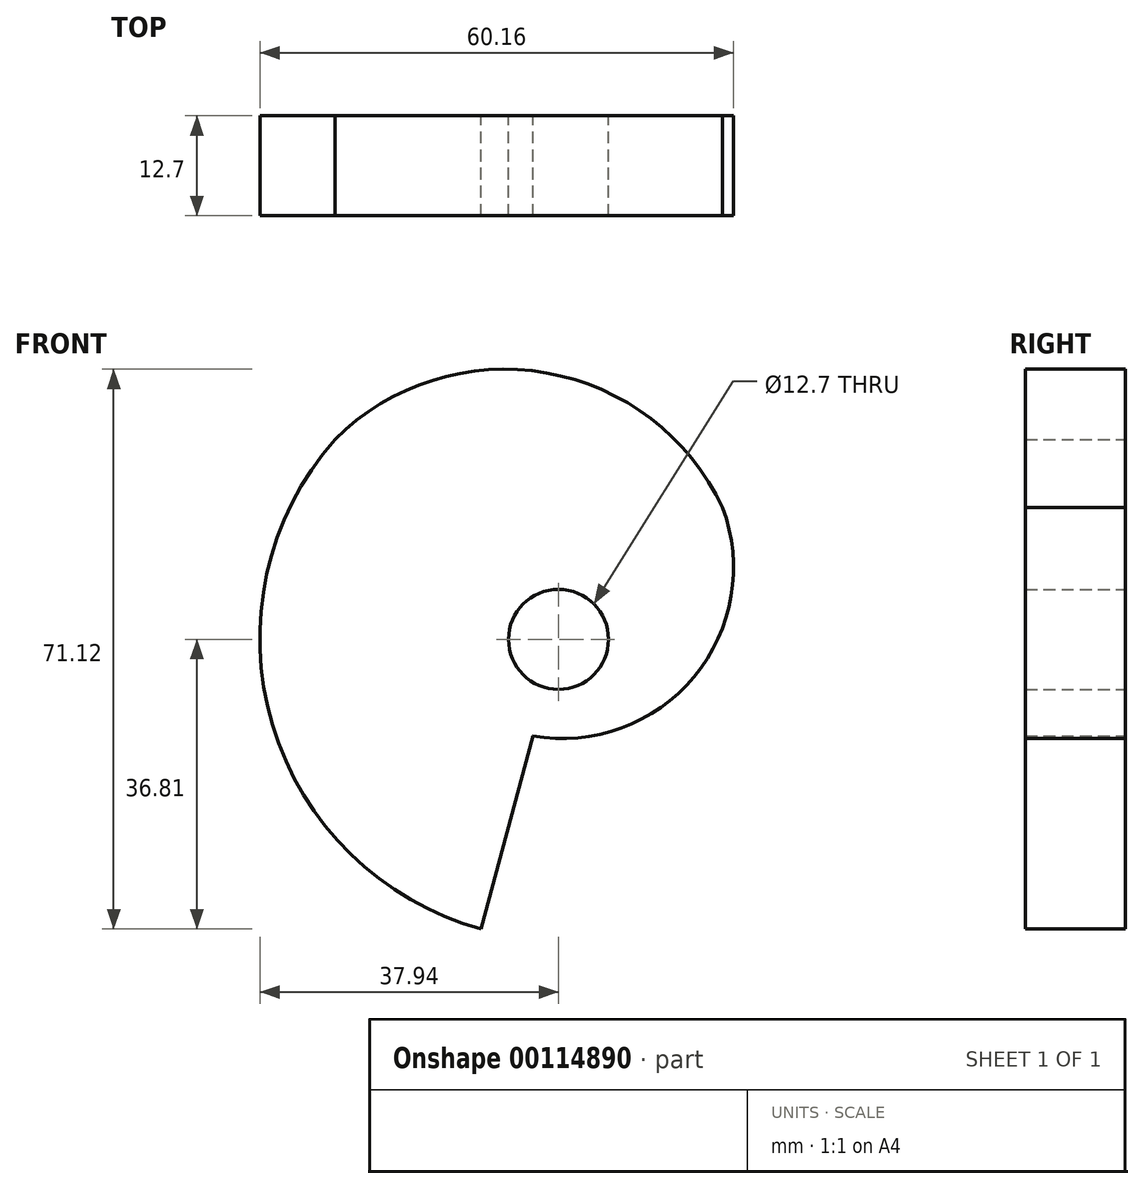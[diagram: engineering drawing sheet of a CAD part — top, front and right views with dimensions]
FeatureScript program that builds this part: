
annotation { "Feature Type Name" : "Feature", "Feature Type Description" : "" }
export const myFeature = defineFeature(function(context is Context, id is Id, definition is map)
    precondition{}
    {
        {
            var Q0;
            Q0=qCreatedBy(makeId("Front.planeOp"),FACE);
            var sketch = newSketch(context, id + "F0", { "sketchPlane" : qUnion([Q0])});
            skCircle(sketch, "E0", {"center": v(0, 0) * mm, "radius": 38.1 * mm, "construction": true});
            skLineSegment(sketch, "E1", {"start": v(-9.82, -36.81) * mm, "end": v(-3.27, -12.27) * mm});
            skArc(sketch, "E2", {"start": v(-28.4, 25.4) * mm, "mid": v(-36.34, -10.86) * mm, "end": v(-9.82, -36.81) * mm});
            skArc(sketch, "E3", {"start": v(20.84, 16.74) * mm, "mid": v(-1.54, 33.85) * mm, "end": v(-28.4, 25.4) * mm});
            skArc(sketch, "E4", {"start": v(-3.27, -12.27) * mm, "mid": v(17.21, -4.77) * mm, "end": v(20.84, 16.74) * mm});
            skSolve(sketch);
        }
        {
            var Q0;
            Q0=makeQuery(id+"F0.imprint","IMPRINT",FACE,{"disambiguationData":[TD([[makeQuery(id+"F0.imprint","IMPRINT",EDGE,{"derivedFrom":sQuery(id+"F0.wireOp",EDGE,"E1")}),1.0]])]});
            var sketch = newSketch(context, id + "F1", { "sketchPlane" : qUnion([Q0])});
            skCircle(sketch, "E5", {"center": v(0, 0) * mm, "radius": 6.35 * mm});
            skSolve(sketch);
        }
        {
            var Q0;
            Q0 = qSketchRegion(id + "F0", true);
            extrude(context, id + "F2", {"entities" : qUnion([Q0]), "depth" : 12.7 * mm});
        }
        {
            var Q0;
            Q0 = qSketchRegion(id + "F1", true);
            extrude(context, id + "F3", {"entities" : qUnion([Q0]), "operationType" : NewBodyOperationType.REMOVE, "depth" : 25.4 * mm});
        }
    });
